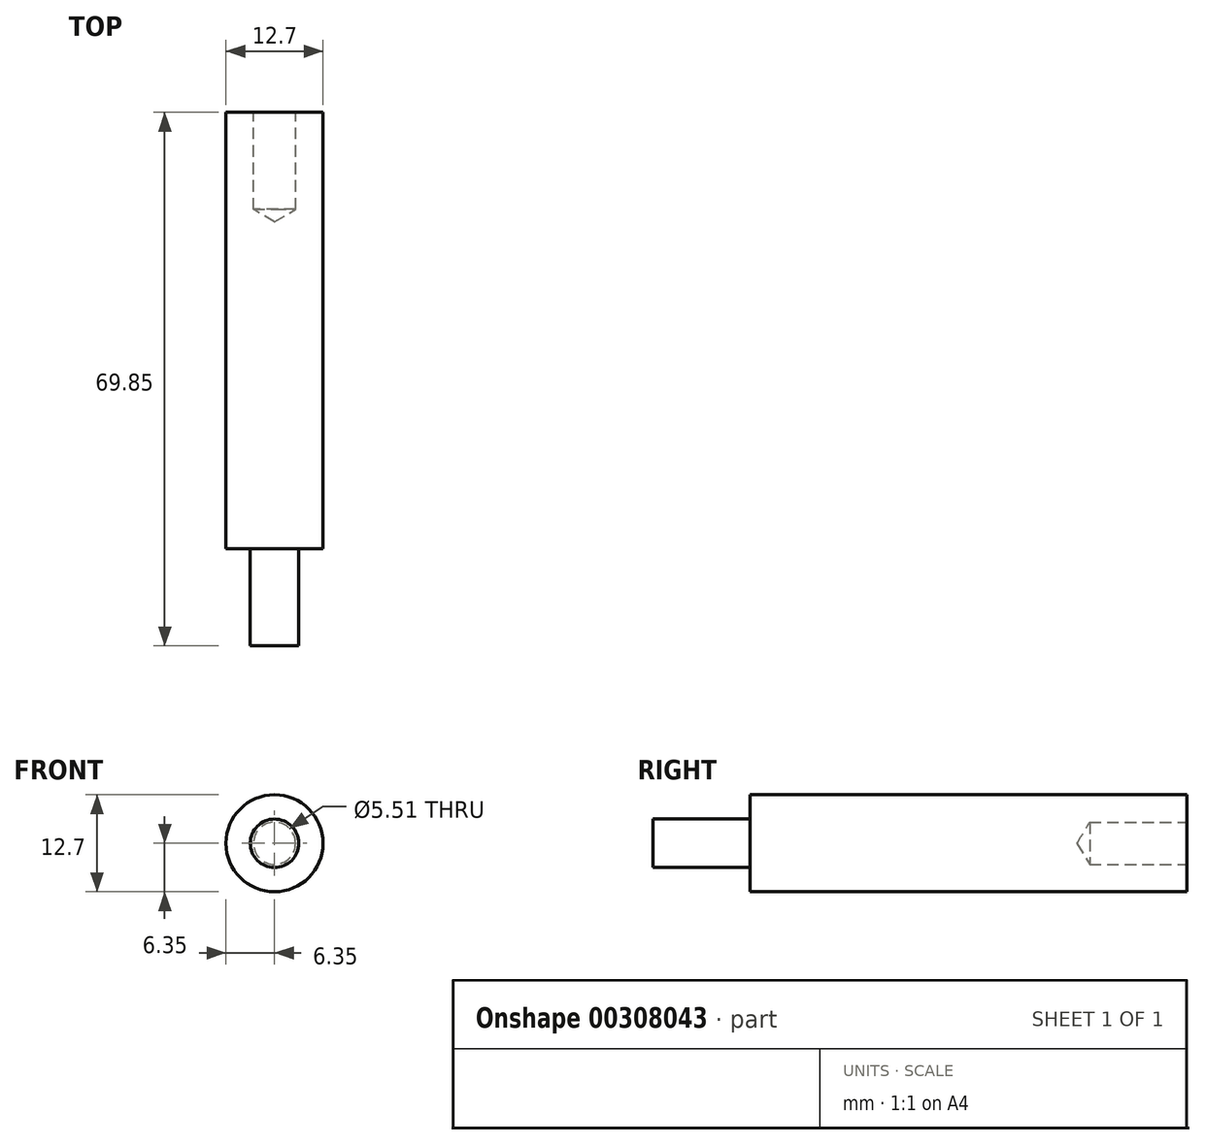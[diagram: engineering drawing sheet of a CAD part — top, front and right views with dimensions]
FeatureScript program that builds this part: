
annotation { "Feature Type Name" : "Feature", "Feature Type Description" : "" }
export const myFeature = defineFeature(function(context is Context, id is Id, definition is map)
    precondition{}
    {
        {
            var Q0;
            Q0=qCreatedBy(makeId("Front.planeOp"),FACE);
            var sketch = newSketch(context, id + "F0", { "sketchPlane" : qUnion([Q0])});
            skCircle(sketch, "E0", {"center": v(0, 0) * mm, "radius": 6.35 * mm});
            skSolve(sketch);
        }
        {
            var Q0;
            Q0 = qSketchRegion(id + "F0", true);
            extrude(context, id + "F1", {"entities" : qUnion([Q0]), "depth" : 57.15 * mm});
        }
        {
            var Q0;
            Q0=makeQuery(id+"F1.opExtrude","CAP_FACE",FACE,{"disambiguationData":[OSD([sQuery(id+"F0.wireOp",EDGE,"E0")])],"isStart":false});
            var sketch = newSketch(context, id + "F2", { "sketchPlane" : qUnion([Q0])});
            skCircle(sketch, "E1", {"center": v(0, 0) * mm, "radius": 3.18 * mm});
            skSolve(sketch);
        }
        {
            var Q0;
            Q0 = qSketchRegion(id + "F2", true);
            extrude(context, id + "F3", {"entities" : qUnion([Q0]), "operationType" : NewBodyOperationType.ADD, "depth" : 12.7 * mm});
        }
        {
            var Q0;
            Q0=makeQuery(id+"F1.opExtrude","CAP_FACE",FACE,{"disambiguationData":[OSD([sQuery(id+"F0.wireOp",EDGE,"E0")])],"isStart":true});
            var sketch = newSketch(context, id + "F4", { "sketchPlane" : qUnion([Q0])});
            skPoint(sketch, "E2", {"position": v(0, 0) * mm});
            skSolve(sketch);
        }
        {
            var Q0;
            Q0=sQuery(id+"F4.wireOp",VERTEX,"E2");
            var Q1;
            Q1=makeQuery(id+"F1.opExtrude","SWEPT_BODY",BODY,{"disambiguationData":[OSD([sQuery(id+"F0.wireOp",EDGE,"E0")])]});
            hole(context, id + "F5", {"style" : HoleStyle.SIMPLE, "endStyle" : HoleEndStyle.BLIND, "holeDiameter" : 5.5 * mm, "holeDepth" : 12.7 * mm, "tappedDepth" : 12.7 * mm, "tapClearance" : 3, "locations" : qUnion([Q0]), "scope" : qUnion([Q1])});
        }
    });
